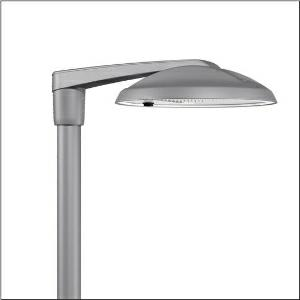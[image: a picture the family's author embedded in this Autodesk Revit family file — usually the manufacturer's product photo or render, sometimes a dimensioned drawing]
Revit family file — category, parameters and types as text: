
# Revit family: dl_50_iq_mini___st1_0a_5xa248d31u08me_7b9a
name_source: partatom
category: Lighting Fixtures
units: mm (PartAtom-declared; Revit-internal decimal feet)

## family parameters
Cut with Voids When Loaded = No
Host = Face
Light Source = No
Part Type = Normal
Room Calculation Point = No
Round Connector Dimension = Use Diameter
Shared = No

## types (1)
- --- (1 x LED, 15720 lm, 107 W, 3000K)
    Apparent Load = 107 VA
    CIE Flux Codes = 37 72 97 100 100
    Color Rendering = 70
    Color Temperature = 3000K
    Default Elevation = 1800 mm
    Description = DL 50 iQ mini, mast luminaire, primary light control with lens, of PMMA, primary optical cover: cover, of toughened safety glass, transparent, light distribution: ST1.0a, light emission: direct distribution, primary light characteristic: asymmetric, installation type: post-top, side-entry, LED, High Power LED, rated luminous flux: 15.720lm, luminous efficacy: 147lm/W, light colour: 730, colour temperature: 3000K, control gear: iQ-Street Remote, D4i with power reduction, control: optimised constant luminous flux control (CLO 2.0), Desk-Remote (wireless, voltage-free reading and setting of iQ features in the workshop via application-optimized NFC function/RFID function), Light-Fading, Smart-Wire, Night-Set, Lumen-Switch, Temp-Guard, Auto-Match, Street-Remote, pre-setting: logarithmic dimming characteristic, mains connection: 220..240V, AC, 50/60Hz, connection cable pre-assembled, cable length: 10,5m, start of lifetime: 107W, end of service life: 113W, reduction: 47W, luminaire housing, of diecast aluminium, powder-coated, SITECO metallic grey (DB 702S), inclination adjustable: 0°, 5°, 10° (post-top) | 0°, -5°, -10°, -15° (side-entry), please order mast post-top element or mast side-entry element separately, diameter: 500mm, height: 115mm, post-top: for spigot size d x l = 76 x 100mm; with reducer (optional accessory) 60 x 100mm | side-entry: for spigot size d x l = 60 x 100mm; with reducer (optional accessory) 42 x 100mm, mounting height: 4..6m, Smart Interface below, protection rating (complete): IP66, insulation class (complete): insulation class II (safety insulation), certification: CE, ENEC, ENEC+, VDE, impact resistance: IK08, permissible operating ambient temperature for outdoor applications: -25..+40°C, standard-compliant lighting for roads and squares, packaging unit: 1 piece

Light Distribution: ST1.0a
    Height = 115 mm
    Lamp = 1 x LED
    Lamp Light Flux = 15720 lm
    Lamp Power = 107 W
    Lamp count = 1
    Length = 500 mm
    Luminous efficacy = 147 lm/W
    Manufacturer = Siteco
    ModVariant = No
    Model = 5XA248D31U08ME
    Number of Poles = 1
    OnlyDefault = Yes
    Power Factor = 1
    Product Name = DL 50 iQ mini | ST1.0a
    Product group = mast luminaire | pylon top
    ProductGroupID = 6100
    Protection Class = Protection class II
    Protection Degree = IP 66
    RLX_Detail_Level = 1
    RLX_Emergency_Light_Flux = 0 lm
    RLX_Emergency_Type = 0
    RLX_Emergency_Type_DB = No
    RlxData = <blob elided: 106437 chars, md5=7f512e28>
    Socket = socket
    Standby Power = 0 W
    System Light Flux = 15720 lm
    System Power = 107 W
    Type Comments = factory setting: luminous flux: 100 % | dim-lin: 254 | 565 mA
    Type Image = l_1296955.jpg
    URL = http://relux.com
    VarID = @adj_073275
    Voltage = 0 V
    Weight = 0.00 kg
    Width = 0 mm  [stored 0 ft]

note: [stored X ft] marks values corroborated as IEEE doubles in the binary element streams (Revit-internal decimal feet)

## geometry (parser evidence)
native form markers: Blend x4, Sweep x9
no freeform markers — native parametric forms only
